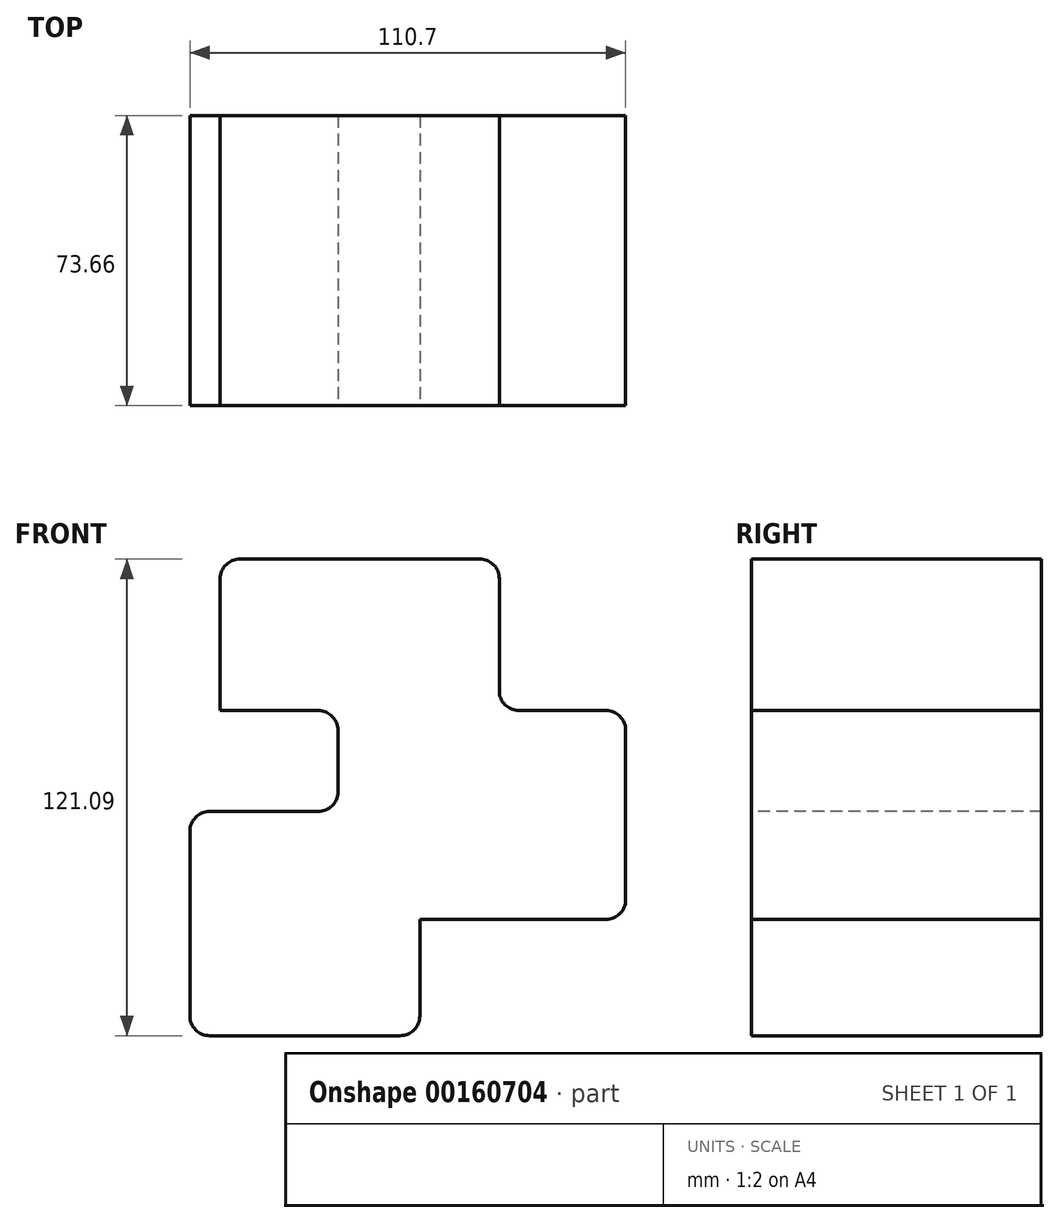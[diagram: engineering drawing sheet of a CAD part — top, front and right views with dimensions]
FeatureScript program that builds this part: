
annotation { "Feature Type Name" : "Feature", "Feature Type Description" : "" }
export const myFeature = defineFeature(function(context is Context, id is Id, definition is map)
    precondition{}
    {
        {
            var Q0;
            Q0=qCreatedBy(makeId("Front.planeOp"),FACE);
            var sketch = newSketch(context, id + "F0", { "sketchPlane" : qUnion([Q0])});
            skLineSegment(sketch, "E0", {"start": v(-32.8, 8.86) * mm, "end": v(-32.8, 47.35) * mm});
            skLineSegment(sketch, "E1", {"start": v(-32.8, 47.35) * mm, "end": v(38.1, 47.35) * mm});
            skLineSegment(sketch, "E2", {"start": v(38.1, 47.35) * mm, "end": v(38.1, 8.86) * mm});
            skLineSegment(sketch, "E3", {"start": v(38.1, 8.86) * mm, "end": v(70.2, 8.86) * mm});
            skLineSegment(sketch, "E4", {"start": v(70.2, 8.86) * mm, "end": v(70.2, -44.2) * mm});
            skLineSegment(sketch, "E5", {"start": v(70.2, -44.2) * mm, "end": v(17.9, -44.2) * mm});
            skLineSegment(sketch, "E6", {"start": v(17.9, -44.2) * mm, "end": v(17.9, -73.74) * mm});
            skLineSegment(sketch, "E7", {"start": v(17.9, -73.74) * mm, "end": v(-40.5, -73.74) * mm});
            skLineSegment(sketch, "E8", {"start": v(-40.5, -73.74) * mm, "end": v(-40.5, -16.8) * mm});
            skLineSegment(sketch, "E9", {"start": v(-40.5, -16.8) * mm, "end": v(-2.9, -16.8) * mm});
            skLineSegment(sketch, "E10", {"start": v(-2.9, -16.8) * mm, "end": v(-2.9, 8.86) * mm});
            skLineSegment(sketch, "E11", {"start": v(-2.9, 8.86) * mm, "end": v(-32.8, 8.86) * mm});
            skSolve(sketch);
        }
        {
            var Q0;
            Q0=makeQuery(id+"F0.imprint","IMPRINT",FACE,{"disambiguationData":[TD([[makeQuery(id+"F0.imprint","IMPRINT",EDGE,{"derivedFrom":sQuery(id+"F0.wireOp",EDGE,"E0")}),-1.0]])]});
            extrude(context, id + "F1", {"entities" : qUnion([Q0]), "oppositeDirection" : true, "depth" : 73.66 * mm});
        }
        {
            var Q0;
            Q0=makeQuery(id+"F1.opExtrude","SWEPT_EDGE",EDGE,{"disambiguationData":[OSD([sQuery(id+"F0.wireOp",EDGE,"E1"),sQuery(id+"F0.wireOp",EDGE,"E2")])]});
            var Q1;
            Q1=makeQuery(id+"F1.opExtrude","SWEPT_EDGE",EDGE,{"disambiguationData":[OSD([sQuery(id+"F0.wireOp",EDGE,"E0"),sQuery(id+"F0.wireOp",EDGE,"E1")])]});
            var Q2;
            Q2=makeQuery(id+"F1.opExtrude","SWEPT_EDGE",EDGE,{"disambiguationData":[OSD([sQuery(id+"F0.wireOp",EDGE,"E2"),sQuery(id+"F0.wireOp",EDGE,"E3")])]});
            var Q3;
            Q3=makeQuery(id+"F1.opExtrude","SWEPT_EDGE",EDGE,{"disambiguationData":[OSD([sQuery(id+"F0.wireOp",EDGE,"E3"),sQuery(id+"F0.wireOp",EDGE,"E4")])]});
            var Q4;
            Q4=makeQuery(id+"F1.opExtrude","SWEPT_EDGE",EDGE,{"disambiguationData":[OSD([sQuery(id+"F0.wireOp",EDGE,"E4"),sQuery(id+"F0.wireOp",EDGE,"E5")])]});
            var Q5;
            Q5=makeQuery(id+"F1.opExtrude","SWEPT_EDGE",EDGE,{"disambiguationData":[OSD([sQuery(id+"F0.wireOp",EDGE,"E6"),sQuery(id+"F0.wireOp",EDGE,"E7")])]});
            var Q6;
            Q6=makeQuery(id+"F1.opExtrude","SWEPT_EDGE",EDGE,{"disambiguationData":[OSD([sQuery(id+"F0.wireOp",EDGE,"E7"),sQuery(id+"F0.wireOp",EDGE,"E8")])]});
            var Q7;
            Q7=makeQuery(id+"F1.opExtrude","SWEPT_EDGE",EDGE,{"disambiguationData":[OSD([sQuery(id+"F0.wireOp",EDGE,"E8"),sQuery(id+"F0.wireOp",EDGE,"E9")])]});
            var Q8;
            Q8=makeQuery(id+"F1.opExtrude","SWEPT_EDGE",EDGE,{"disambiguationData":[OSD([sQuery(id+"F0.wireOp",EDGE,"E9"),sQuery(id+"F0.wireOp",EDGE,"E10")])]});
            var Q9;
            Q9=makeQuery(id+"F1.opExtrude","SWEPT_EDGE",EDGE,{"disambiguationData":[OSD([sQuery(id+"F0.wireOp",EDGE,"E10"),sQuery(id+"F0.wireOp",EDGE,"E11")])]});
            fillet(context, id + "F2", {"entities" : qUnion([Q0, Q1, Q2, Q3, Q4, Q5, Q6, Q7, Q8, Q9]), "radius" : 5 * mm, "tangentPropagation" : true, "allowEdgeOverflow" : false});
        }
    });
